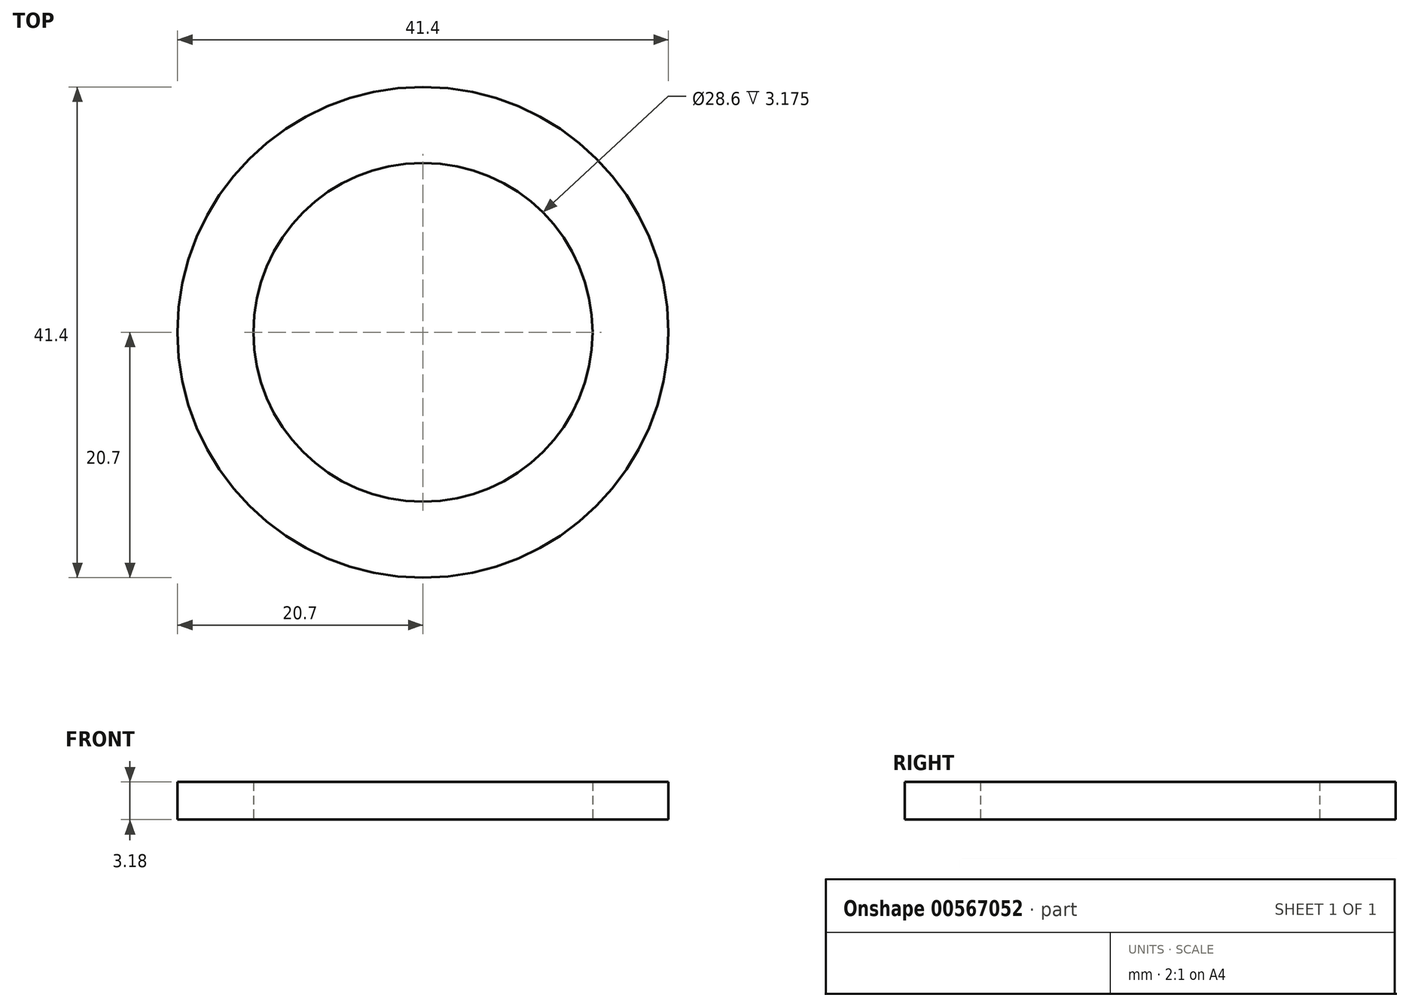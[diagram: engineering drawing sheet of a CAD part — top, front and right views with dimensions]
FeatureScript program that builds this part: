
annotation { "Feature Type Name" : "Feature", "Feature Type Description" : "" }
export const myFeature = defineFeature(function(context is Context, id is Id, definition is map)
    precondition{}
    {
        {
            var Q0;
            Q0=qCreatedBy(makeId("Top.planeOp"),FACE);
            var sketch = newSketch(context, id + "F0", { "sketchPlane" : qUnion([Q0])});
            skCircle(sketch, "E0", {"center": v(0, 0) * mm, "radius": 20.7 * mm});
            skCircle(sketch, "E1", {"center": v(0, 0) * mm, "radius": 14.3 * mm});
            skSolve(sketch);
        }
        {
            var Q0;
            Q0=makeQuery(id+"F0.imprint","IMPRINT",FACE,{"disambiguationData":[TD([[makeQuery(id+"F0.imprint","IMPRINT",EDGE,{"derivedFrom":sQuery(id+"F0.wireOp",EDGE,"E0")}),1.0]])]});
            extrude(context, id + "F1", {"entities" : qUnion([Q0]), "depth" : 3.17 * mm, "offsetDistance" : 25.4 * mm});
        }
    });
